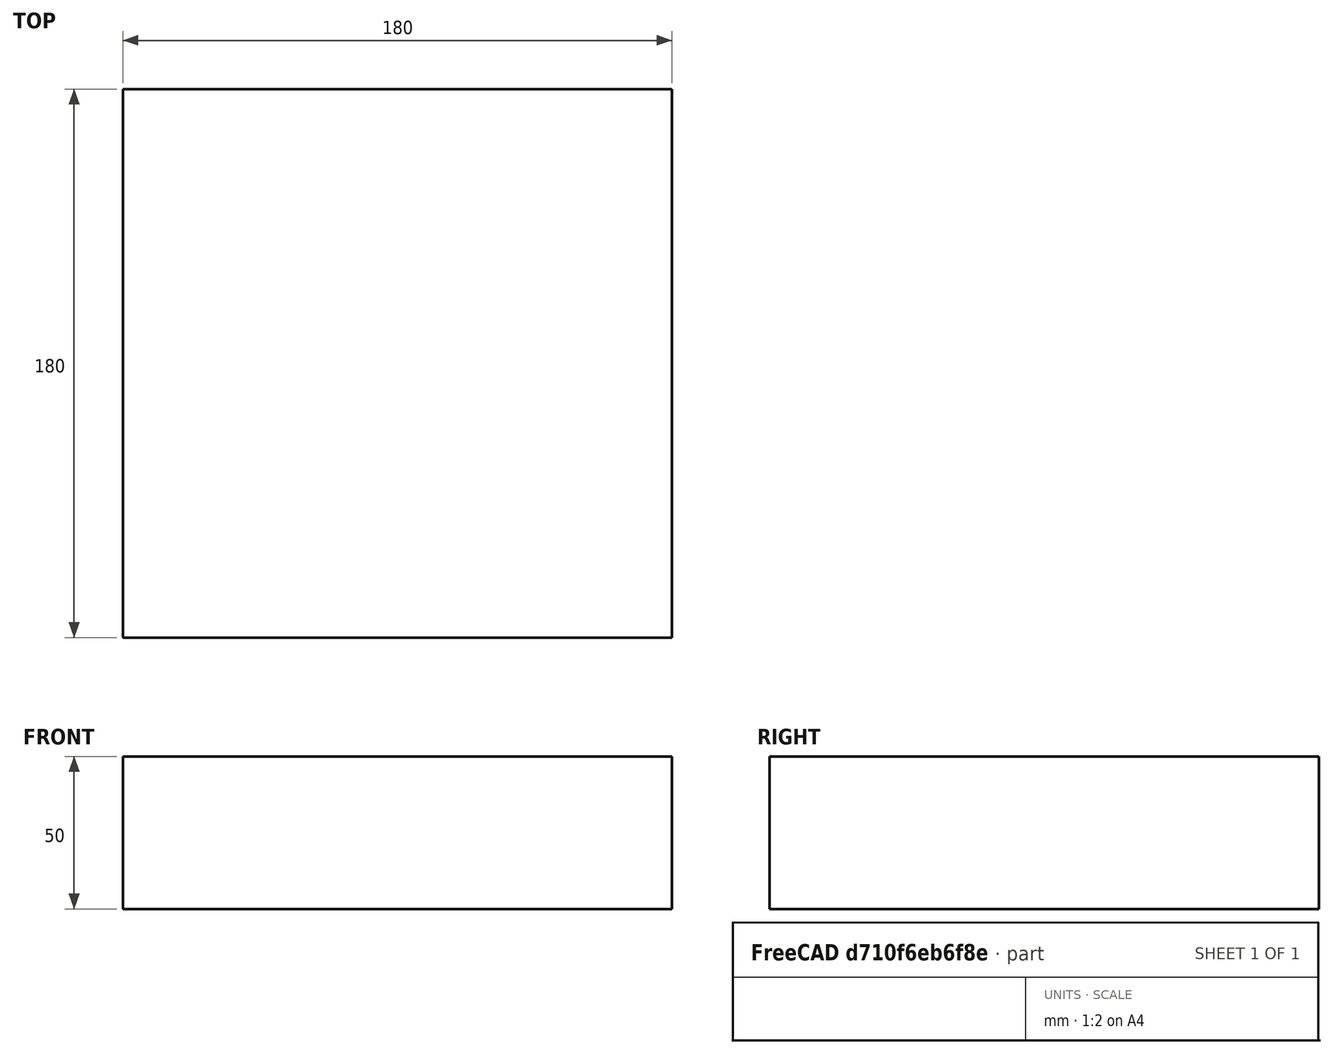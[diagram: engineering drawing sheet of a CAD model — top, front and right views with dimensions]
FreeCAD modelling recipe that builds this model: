
FCSTD DOCUMENT  (FreeCAD 0.15R4671 (Git))
Label: Square Bar 180 EN10059 S235JR
License: All rights reserved
LicenseURL: http://en.wikipedia.org/wiki/All_rights_reserved
objects: Sketcher::SketchObject×1, Part::Extrusion×1
note: 2 computed .brp shape members not serialized (recipe doc carries the construction recipe); baked Part::Feature solids carry a one-line shape summary decoded from their .brp

FEATURE [Sketcher::SketchObject] Sketch
  sketch-geometry (4):
    g0: LineSegment StartX=-90 StartY=-90 StartZ=0 EndX=90 EndY=-90 EndZ=0
    g1: LineSegment StartX=90 StartY=-90 StartZ=0 EndX=90 EndY=90 EndZ=0
    g2: LineSegment StartX=90 StartY=90 StartZ=0 EndX=-90 EndY=90 EndZ=0
    g3: LineSegment StartX=-90 StartY=90 StartZ=0 EndX=-90 EndY=-90 EndZ=0
  constraints (12):
    c: Coincident(g0,g1)
    c: Coincident(g1,g2)
    c: Coincident(g2,g3)
    c: Coincident(g3,g0)
    c: Horizontal(g0)
    c: Horizontal(g2)
    c: Vertical(g1)
    c: Vertical(g3)
    c: Symmetric(g1,g0,g-1)
    c: Symmetric(g2,g1,g-2)
    c: Equal(g1,g2)
    c: DistanceY(g1) = 180
FEATURE [Part::Extrusion] Extrude  label="Square Bar 180 EN10059 S235JR"
  Base = -> Sketch
  Dir = (0,0,50)
  Solid = true
